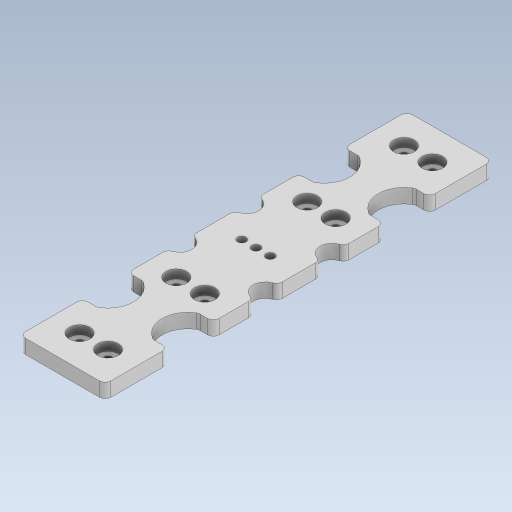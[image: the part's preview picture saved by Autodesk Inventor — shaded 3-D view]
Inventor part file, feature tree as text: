
AUTODESK INVENTOR PART (.ipt)
format: ipt  version: 2023.5 (Build 275446000, 446)  size: 514,560 bytes
history: native  units: mm
features: extrude x2, sketch x1
ambient origin geometry x8: Origin, YZ Plane, XZ Plane, XY Plane, X Axis, Y Axis, Z Axis, Center Point
bodies: Solid1 (feature_tree)
feature tree (3):
  sketch  "Sketch1"  dims[d0=15.0mm d1=7.5mm d2=7.3mm d3=23.0mm d4=10.0mm d5=7.3mm d6=10.0mm d7=34.0mm d8=4.0mm d9=4.0mm d10=2.0mm d11=2.0mm d12=2.0mm d13=2.0mm d14=2.0mm d15=5.0mm d16=0.0mm d17=2.0mm d18=0.0mm d19=3.0mm d20=3.0mm d21=3.0mm d22=3.0mm d23=3.0mm d24=3.0mm d25=3.0mm d26=3.0mm d27=3.0mm d28=3.0mm d29=3.0mm]
  extrude  "Extrusion1"  Depth=5.0mm TaperAngle=0.0deg
  extrude  "Extrusion2"  Depth=2.0mm TaperAngle=0.0deg
